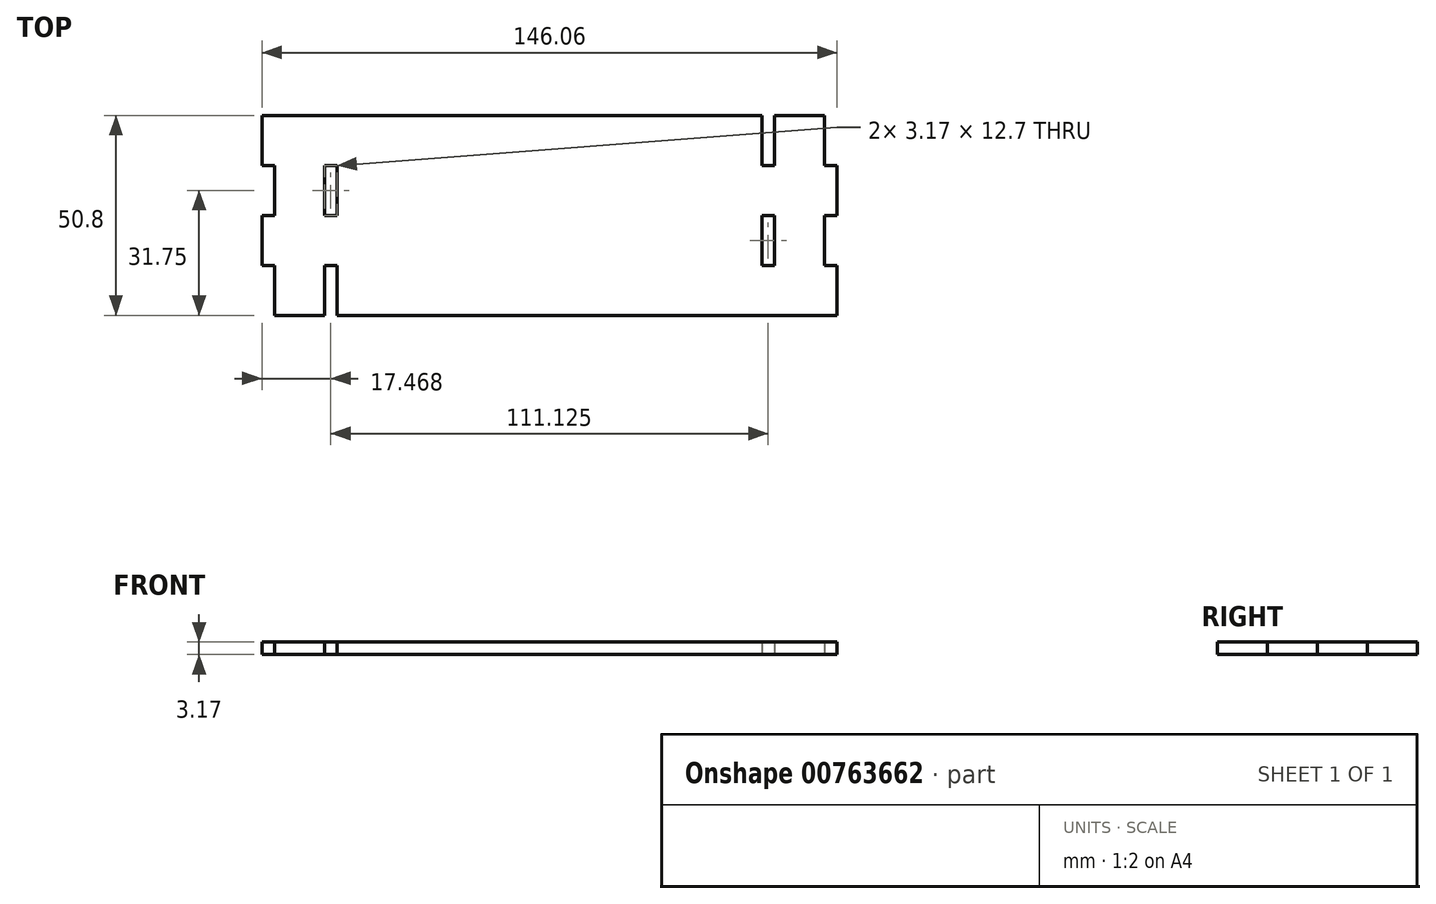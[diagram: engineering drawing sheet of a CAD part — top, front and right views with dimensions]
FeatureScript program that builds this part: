
annotation { "Feature Type Name" : "Feature", "Feature Type Description" : "" }
export const myFeature = defineFeature(function(context is Context, id is Id, definition is map)
    precondition{}
    {
        {
            var Q0;
            Q0=qCreatedBy(makeId("Top.planeOp"),FACE);
            var sketch = newSketch(context, id + "F0", { "sketchPlane" : qUnion([Q0])});
            skLineSegment(sketch, "E0.bottom", {"start": v(73.03, 25.4) * mm, "end": v(-73.03, 25.4) * mm});
            skLineSegment(sketch, "E0.top", {"start": v(73.03, -25.4) * mm, "end": v(-73.03, -25.4) * mm});
            skLineSegment(sketch, "E0.left", {"start": v(73.03, 25.4) * mm, "end": v(73.03, -25.4) * mm});
            skLineSegment(sketch, "E0.right", {"start": v(-73.03, 25.4) * mm, "end": v(-73.03, -25.4) * mm});
            skPoint(sketch, "E0.middle", {"position": v(0, 0) * mm});
            skLineSegment(sketch, "E1.bottom", {"start": v(-73.03, -25.4) * mm, "end": v(-69.85, -25.4) * mm});
            skLineSegment(sketch, "E1.top", {"start": v(-73.03, -12.7) * mm, "end": v(-69.85, -12.7) * mm});
            skLineSegment(sketch, "E1.left", {"start": v(-73.03, -25.4) * mm, "end": v(-73.03, -12.7) * mm});
            skLineSegment(sketch, "E1.right", {"start": v(-69.85, -25.4) * mm, "end": v(-69.85, -12.7) * mm});
            skLineSegment(sketch, "E2.0.1.0", {"start": v(-73.03, 12.7) * mm, "end": v(-69.85, 12.7) * mm});
            skLineSegment(sketch, "E2.0.1.1", {"start": v(-73.03, 0) * mm, "end": v(-69.85, 0) * mm});
            skLineSegment(sketch, "E2.0.1.2", {"start": v(-73.03, 0) * mm, "end": v(-73.03, 12.7) * mm});
            skLineSegment(sketch, "E2.0.1.3", {"start": v(-69.85, 0) * mm, "end": v(-69.85, 12.7) * mm});
            skLineSegment(sketch, "E2.1.0.0", {"start": v(-57.15, -12.7) * mm, "end": v(-53.98, -12.7) * mm});
            skLineSegment(sketch, "E2.1.0.1", {"start": v(-57.15, -25.4) * mm, "end": v(-53.98, -25.4) * mm});
            skLineSegment(sketch, "E2.1.0.2", {"start": v(-57.15, -25.4) * mm, "end": v(-57.15, -12.7) * mm});
            skLineSegment(sketch, "E2.1.0.3", {"start": v(-53.98, -25.4) * mm, "end": v(-53.98, -12.7) * mm});
            skLineSegment(sketch, "E2.1.1.0", {"start": v(-57.15, 12.7) * mm, "end": v(-53.98, 12.7) * mm});
            skLineSegment(sketch, "E2.1.1.1", {"start": v(-57.15, 0) * mm, "end": v(-53.98, 0) * mm});
            skLineSegment(sketch, "E2.1.1.2", {"start": v(-57.15, 0) * mm, "end": v(-57.15, 12.7) * mm});
            skLineSegment(sketch, "E2.1.1.3", {"start": v(-53.98, 0) * mm, "end": v(-53.98, 12.7) * mm});
            skLineSegment(sketch, "E2.direction1", {"start": v(-73.03, -25.4) * mm, "end": v(-57.15, -25.4) * mm, "construction": true});
            skLineSegment(sketch, "E2.direction2", {"start": v(-73.03, -25.4) * mm, "end": v(-73.03, 0) * mm, "construction": true});
            skLineSegment(sketch, "E3.bottom", {"start": v(73.03, 25.4) * mm, "end": v(69.85, 25.4) * mm});
            skLineSegment(sketch, "E3.top", {"start": v(73.03, 12.7) * mm, "end": v(69.85, 12.7) * mm});
            skLineSegment(sketch, "E3.left", {"start": v(73.03, 25.4) * mm, "end": v(73.03, 12.7) * mm});
            skLineSegment(sketch, "E3.right", {"start": v(69.85, 25.4) * mm, "end": v(69.85, 12.7) * mm});
            skLineSegment(sketch, "E4.0.1.0", {"start": v(73.03, 0) * mm, "end": v(73.03, -12.7) * mm});
            skLineSegment(sketch, "E4.0.1.1", {"start": v(69.85, 0) * mm, "end": v(69.85, -12.7) * mm});
            skLineSegment(sketch, "E4.0.1.2", {"start": v(73.03, -12.7) * mm, "end": v(69.85, -12.7) * mm});
            skLineSegment(sketch, "E4.0.1.3", {"start": v(73.03, 0) * mm, "end": v(69.85, 0) * mm});
            skLineSegment(sketch, "E4.1.0.0", {"start": v(57.15, 25.4) * mm, "end": v(57.15, 12.7) * mm});
            skLineSegment(sketch, "E4.1.0.1", {"start": v(53.98, 25.4) * mm, "end": v(53.98, 12.7) * mm});
            skLineSegment(sketch, "E4.1.0.2", {"start": v(57.15, 12.7) * mm, "end": v(53.98, 12.7) * mm});
            skLineSegment(sketch, "E4.1.0.3", {"start": v(57.15, 25.4) * mm, "end": v(53.98, 25.4) * mm});
            skLineSegment(sketch, "E4.1.1.0", {"start": v(57.15, 0) * mm, "end": v(57.15, -12.7) * mm});
            skLineSegment(sketch, "E4.1.1.1", {"start": v(53.98, 0) * mm, "end": v(53.98, -12.7) * mm});
            skLineSegment(sketch, "E4.1.1.2", {"start": v(57.15, -12.7) * mm, "end": v(53.98, -12.7) * mm});
            skLineSegment(sketch, "E4.1.1.3", {"start": v(57.15, 0) * mm, "end": v(53.98, 0) * mm});
            skLineSegment(sketch, "E4.direction1", {"start": v(69.85, 12.7) * mm, "end": v(53.98, 12.7) * mm, "construction": true});
            skLineSegment(sketch, "E4.direction2", {"start": v(69.85, 12.7) * mm, "end": v(69.85, -12.7) * mm, "construction": true});
            skSolve(sketch);
        }
        {
            var Q0;
            {var subQ21=sQuery(id+"F0.wireOp",EDGE,"E1.top");Q0=makeQuery(id+"F0.imprint","IMPRINT",FACE,{"disambiguationData":[TD([[makeQuery(id+"F0.imprint","IMPRINT",EDGE,{"derivedFrom":subQ21}),1.0]])]});}
            extrude(context, id + "F1", {"entities" : qUnion([Q0]), "depth" : 3.17 * mm, "offsetDistance" : 25.4 * mm});
        }
    });
